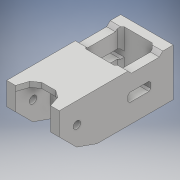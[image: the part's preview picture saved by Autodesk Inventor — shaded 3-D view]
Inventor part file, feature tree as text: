
AUTODESK INVENTOR PART (.ipt)
format: ipt  version: 2018 (Build 220112000, 112)  size: 322,560 bytes
history: native  units: mm
features: extrude x13, sketch x12, chamfer x5, projected_geometry x4
ambient origin geometry x8: Origin, YZ Plane, XZ Plane, XY Plane, X Axis, Y Axis, Z Axis, Center Point
bodies: Solid1 (feature_tree)
feature tree (34):
  extrude  "Extrusion1"  Depth=21.9mm
  extrude  "Extrusion2"  Depth=5.0mm
  extrude  "Extrusion3"  Depth=18.1mm
  extrude  "Extrusion4"  Depth=27.0mm TaperAngle=0.0deg
  extrude  "Extrusion5"  Depth=7.0mm
  extrude  "Extrusion6"  Depth=20.0mm
  chamfer  "Chamfer1"  Distance=14.0mm
  extrude  "Extrusion7"  Depth=5.0mm
  extrude  "Extrusion8"  Depth=20.0mm TaperAngle=0.0deg
  chamfer  "Chamfer2"  Distance=8.0mm
  extrude  "Extrusion9"  Depth=1.0mm TaperAngle=45.0deg
  chamfer  "Chamfer3"  Distance=4.0mm
  extrude  "Extrusion10"  Depth=2.0mm
  extrude  "Extrusion11"  Depth=10.0mm
  extrude  "Extrusion12"  Depth=15.0mm
  chamfer  "Chamfer4"  Distance=4.0mm
  extrude  "Extrusion13"  Depth=9.0mm
  chamfer  "Chamfer5"  Distance=3.0mm
  sketch  "Sketch1"  dims[d0=20.0mm d1=21.9mm]
  sketch  "Sketch3"  dims[d2=5.0mm d3=5.0mm]
  sketch  "Sketch4"  dims[d4=5.0mm d5=18.1mm]
  sketch  "Sketch5"  dims[d6=20.0mm d7=27.0mm d8=0.0mm]
  sketch  "Sketch6"  dims[d9=5.2mm d10=7.0mm]
  projected_geometry  "Projected Loop1"
  sketch  "Sketch8"  dims[d11=20.0mm d12=0.0mm d13=9.3mm]
  sketch  "Sketch9"  dims[d14=8.3mm]
  projected_geometry  "Projected Loop2"
  sketch  "Sketch10"  dims[d15=8.3mm d16=14.0mm d17=0.0mm]
  projected_geometry  "Projected Loop3"
  sketch  "Sketch11"  dims[d18=3.0mm d19=0.0mm d20=5.0mm]
  sketch  "Sketch12"  dims[d21=12.0mm d23=20.0mm d24=0.0mm]
  sketch  "Sketch13"  dims[d25=5.0mm]
  projected_geometry  "Projected Loop4"
  sketch  "Sketch14"  dims[d26=13.0mm d27=8.0mm d28=0.0mm d29=1.0mm d30=2.0mm d31=45.0deg d32=4.0mm d33=4.2mm d34=10.0mm d35=15.0mm d36=4.0mm d37=0.0mm d38=9.0mm d39=3.0mm d40=4.0mm d41=0.0mm d42=3.0mm d43=2.0mm d44=45.0deg d45=6.5mm d46=12.0mm d47=10.0mm d48=0.0mm d49=4.0mm d50=2.0mm d51=45.0deg d52=13.0mm d53=9.0mm d54=12.0mm d55=0.0mm d56=45.0deg d57=14.0mm d58=4.1mm d59=7.5mm d60=12.0mm d61=0.0mm d62=1.0mm d63=2.0mm d64=12.0mm d65=0.0mm d66=2.0mm d67=2.0mm d68=45.0deg d69=45.0deg d70=4.0mm d71=0.0mm d73=1.0mm d74=0.0mm d75=3.0mm d76=3.0mm d77=2.0mm d78=2.0mm d79=45.0deg]
